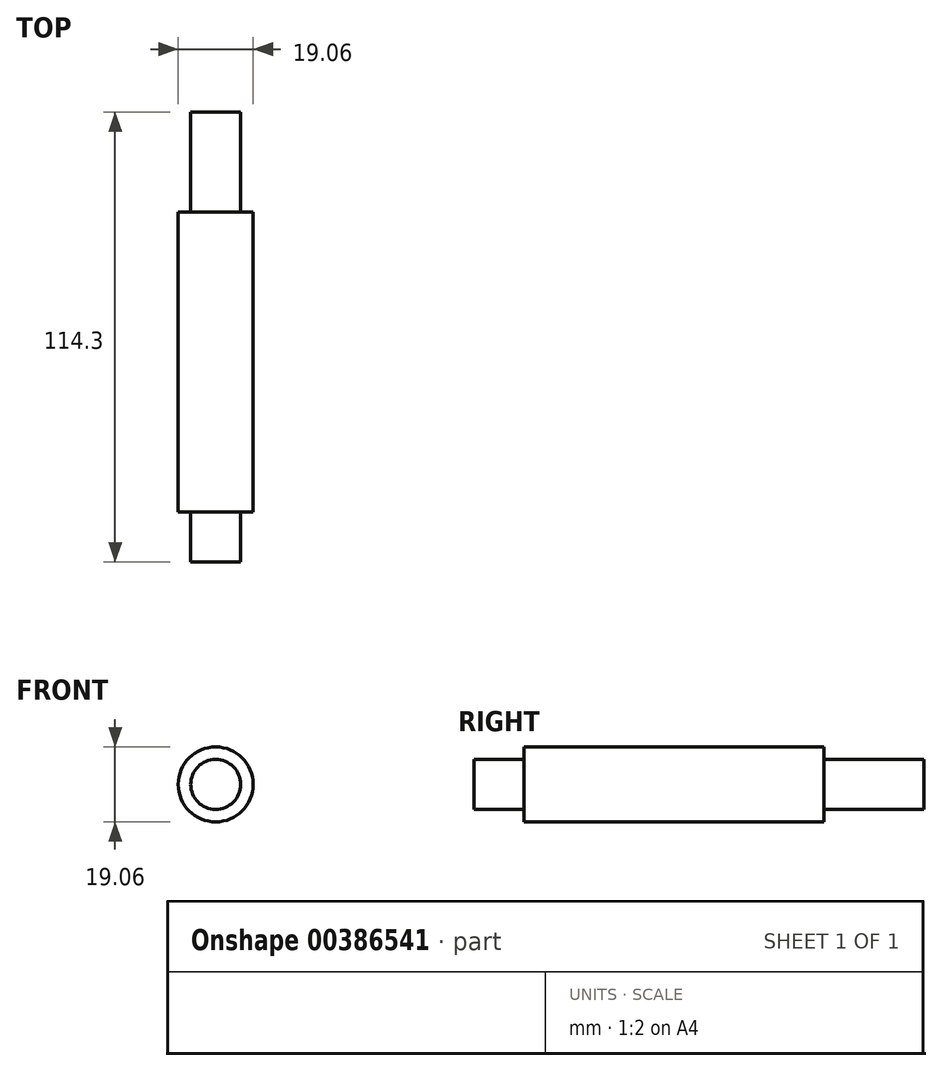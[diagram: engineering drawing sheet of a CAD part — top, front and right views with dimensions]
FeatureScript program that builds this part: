
annotation { "Feature Type Name" : "Feature", "Feature Type Description" : "" }
export const myFeature = defineFeature(function(context is Context, id is Id, definition is map)
    precondition{}
    {
        {
            var Q0;
            Q0=qCreatedBy(makeId("Front.planeOp"),FACE);
            var sketch = newSketch(context, id + "F0", { "sketchPlane" : qUnion([Q0])});
            skCircle(sketch, "E0", {"center": v(0, 0) * mm, "radius": 9.53 * mm});
            skCircle(sketch, "E1", {"center": v(0, 0) * mm, "radius": 6.35 * mm});
            skSolve(sketch);
        }
        {
            var Q0;
            Q0=makeQuery(id+"F0.imprint","IMPRINT",FACE,{"disambiguationData":[TD([[makeQuery(id+"F0.imprint","IMPRINT",EDGE,{"derivedFrom":sQuery(id+"F0.wireOp",EDGE,"E0")}),1.0]])]});
            var Q1;
            Q1=makeQuery(id+"F0.imprint","IMPRINT",FACE,{"disambiguationData":[TD([[makeQuery(id+"F0.imprint","IMPRINT",EDGE,{"derivedFrom":sQuery(id+"F0.wireOp",EDGE,"E1")}),1.0]])]});
            extrude(context, id + "F1", {"entities" : qUnion([Q0, Q1]), "depth" : 76.2 * mm});
        }
        {
            var Q0;
            Q0=makeQuery(id+"F1.opExtrude","CAP_FACE",FACE,{"disambiguationData":[OSD([sQuery(id+"F0.wireOp",EDGE,"E0")])],"isStart":false});
            var sketch = newSketch(context, id + "F2", { "sketchPlane" : qUnion([Q0])});
            skCircle(sketch, "E2", {"center": v(0, 0) * mm, "radius": 6.35 * mm});
            skSolve(sketch);
        }
        {
            var Q0;
            Q0 = qSketchRegion(id + "F2", true);
            extrude(context, id + "F3", {"entities" : qUnion([Q0]), "operationType" : NewBodyOperationType.ADD, "depth" : 12.7 * mm});
        }
        {
            var Q0;
            Q0=makeQuery(id+"F1.opExtrude","CAP_FACE",FACE,{"disambiguationData":[OSD([sQuery(id+"F0.wireOp",EDGE,"E0")])],"isStart":true});
            var sketch = newSketch(context, id + "F4", { "sketchPlane" : qUnion([Q0])});
            skCircle(sketch, "E3", {"center": v(0, 0) * mm, "radius": 6.35 * mm});
            skSolve(sketch);
        }
        {
            var Q0;
            Q0 = qSketchRegion(id + "F4", true);
            extrude(context, id + "F5", {"entities" : qUnion([Q0]), "operationType" : NewBodyOperationType.ADD, "depth" : 25.4 * mm});
        }
    });
